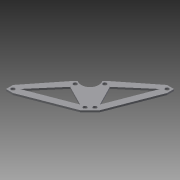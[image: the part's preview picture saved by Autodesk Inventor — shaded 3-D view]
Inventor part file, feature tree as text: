
AUTODESK INVENTOR PART (.ipt)
format: ipt  version: 2013 (Build 170138000, 138)  size: 111,616 bytes
history: native  units: in
note: dims shown in document units (in); Inventor stores cm internally (conversion verified against a paired STEP export)
features: extrude x1, sketch x1
ambient origin geometry x8: Origin, YZ Plane, XZ Plane, XY Plane, X Axis, Y Axis, Z Axis, Center Point
bodies: Solid1 (feature_tree)
feature tree (2):
  extrude  "Extrusion1"  Depth=0.266in
  sketch  "Sketch1"  dims[d8=0.266in d9=0.266in d10=1.5in d12=0.75in d13=0.35in d14=0.35in d15=0.25in d17=0.25in d20=0.25in d21=0.25in d25=0.25in d26=0.5in d27=0.5in d28=0.125in d29=0.0in d30=1.25in]
